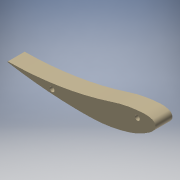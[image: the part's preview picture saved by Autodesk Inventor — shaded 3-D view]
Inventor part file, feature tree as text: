
AUTODESK INVENTOR PART (.ipt)
format: ipt  version: 2018 (Build 220112000, 112)  size: 114,176 bytes
history: native  units: mm
features: extrude x1, sketch x1, projected_geometry x1
ambient origin geometry x8: Origin, YZ Plane, XZ Plane, XY Plane, X Axis, Y Axis, Z Axis, Center Point
bodies: Body1 (feature_tree)
feature tree (3):
  extrude  "押し出し1"  Depth=41.5mm TaperAngle=0.0deg
  sketch  "スケッチ1"
  projected_geometry  "投影ループ1"
